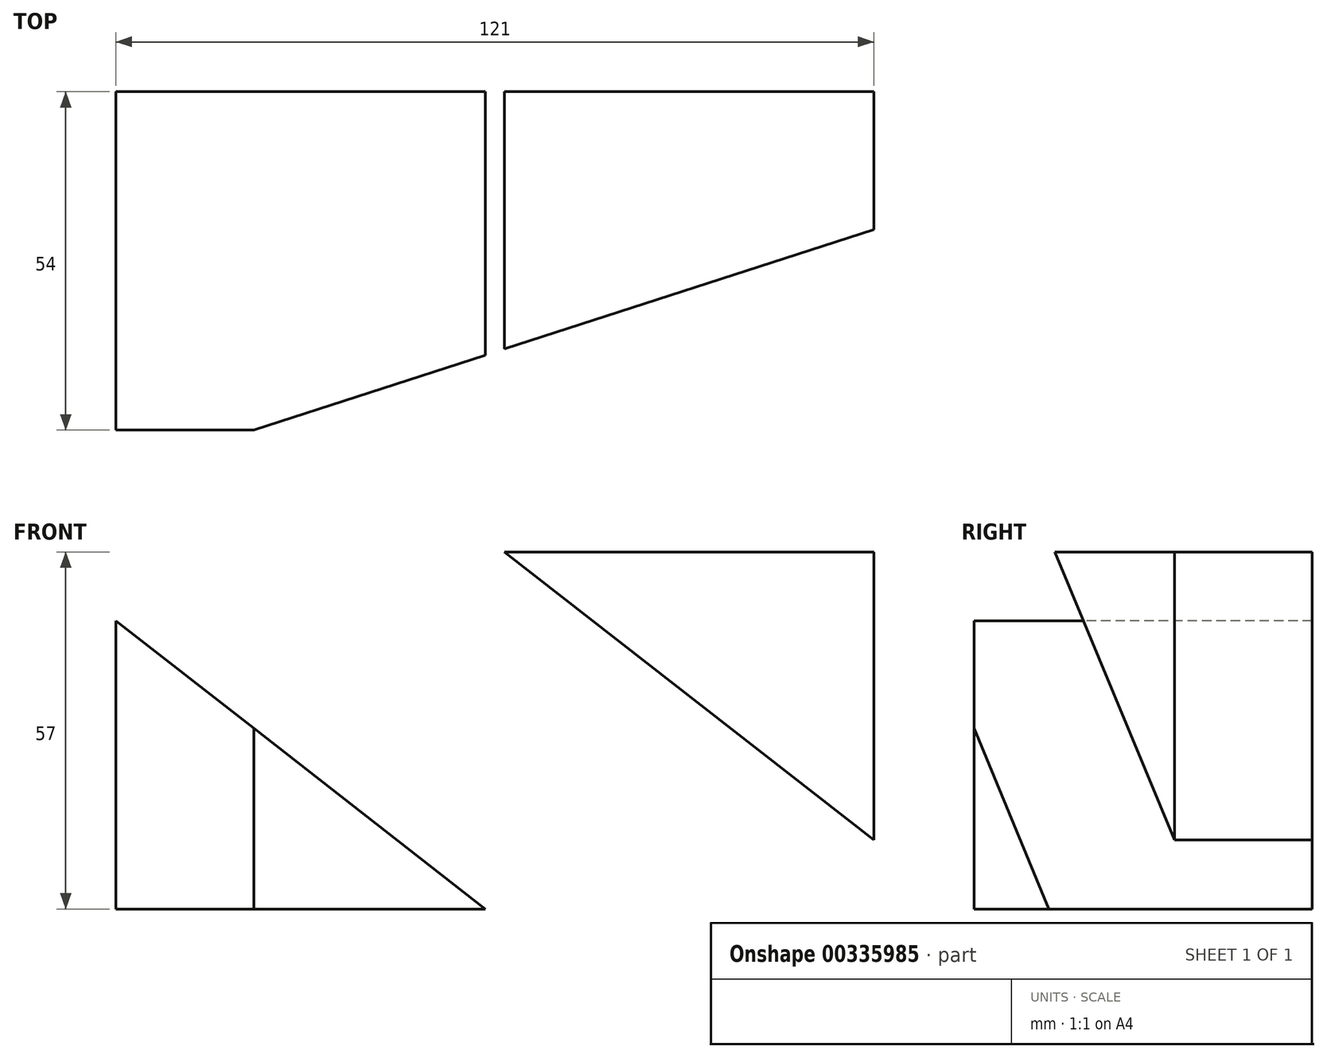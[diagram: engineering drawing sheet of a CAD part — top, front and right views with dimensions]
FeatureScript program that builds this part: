
annotation { "Feature Type Name" : "Feature", "Feature Type Description" : "" }
export const myFeature = defineFeature(function(context is Context, id is Id, definition is map)
    precondition{}
    {
        {
            var Q0;
            Q0=qCreatedBy(makeId("Front.planeOp"),FACE);
            var sketch = newSketch(context, id + "F0", { "sketchPlane" : qUnion([Q0])});
            skLineSegment(sketch, "E0", {"start": v(0, 0) * mm, "end": v(0, 57) * mm});
            skLineSegment(sketch, "E1", {"start": v(0, 0) * mm, "end": v(22, 0) * mm});
            skLineSegment(sketch, "E2", {"start": v(0, 57) * mm, "end": v(62, 57) * mm});
            skLineSegment(sketch, "E3", {"start": v(62, 57) * mm, "end": v(121, 57) * mm});
            skLineSegment(sketch, "E4", {"start": v(121, 57) * mm, "end": v(121, 11) * mm});
            skLineSegment(sketch, "E5", {"start": v(0, 0) * mm, "end": v(0, 46) * mm});
            skLineSegment(sketch, "E6", {"start": v(0, 46) * mm, "end": v(59, 0) * mm});
            skLineSegment(sketch, "E7", {"start": v(22, 0) * mm, "end": v(59, 0) * mm});
            skLineSegment(sketch, "E8", {"start": v(121, 11) * mm, "end": v(121, 0) * mm});
            skLineSegment(sketch, "E9", {"start": v(121, 0) * mm, "end": v(59, 0) * mm});
            skLineSegment(sketch, "E10", {"start": v(62, 57) * mm, "end": v(121, 11) * mm});
            skLineSegment(sketch, "E11", {"start": v(22, 0) * mm, "end": v(22, 28.85) * mm});
            skSolve(sketch);
        }
        {
            var Q0;
            Q0=makeQuery(id+"F0.imprint","IMPRINT",FACE,{"disambiguationData":[TD([[makeQuery(id+"F0.imprint","IMPRINT",EDGE,{"derivedFrom":sQuery(id+"F0.wireOp",EDGE,"E1")}),1.0]])]});
            var Q1;
            {var subQ0=sQuery(id+"F0.wireOp",EDGE,"E7");Q1=makeQuery(id+"F0.imprint","IMPRINT",FACE,{"disambiguationData":[TD([[makeQuery(id+"F0.imprint","IMPRINT",EDGE,{"derivedFrom":subQ0}),1.0]])]});}
            var Q2;
            {var subQ1=sQuery(id+"F0.wireOp",EDGE,"E0");Q2=makeQuery(id+"F0.imprint","IMPRINT",FACE,{"disambiguationData":[TD([[makeQuery(id+"F0.imprint","IMPRINT",EDGE,{"derivedFrom":subQ1}),-1.0]])]});}
            var Q3;
            Q3=makeQuery(id+"F0.imprint","IMPRINT",FACE,{"disambiguationData":[TD([[makeQuery(id+"F0.imprint","IMPRINT",EDGE,{"derivedFrom":sQuery(id+"F0.wireOp",EDGE,"E3")}),-1.0]])]});
            extrude(context, id + "F1", {"entities" : qUnion([Q0, Q1, Q2, Q3]), "oppositeDirection" : true, "depth" : 16 * mm});
        }
        {
            var Q0;
            Q0=makeQuery(id+"F0.imprint","IMPRINT",FACE,{"disambiguationData":[TD([[makeQuery(id+"F0.imprint","IMPRINT",EDGE,{"derivedFrom":sQuery(id+"F0.wireOp",EDGE,"E3")}),-1.0]])]});
            var Q1;
            {var subQ0=sQuery(id+"F0.wireOp",EDGE,"E7");Q1=makeQuery(id+"F0.imprint","IMPRINT",FACE,{"disambiguationData":[TD([[makeQuery(id+"F0.imprint","IMPRINT",EDGE,{"derivedFrom":subQ0}),1.0]])]});}
            var Q2;
            Q2=makeQuery(id+"F0.imprint","IMPRINT",FACE,{"disambiguationData":[TD([[makeQuery(id+"F0.imprint","IMPRINT",EDGE,{"derivedFrom":sQuery(id+"F0.wireOp",EDGE,"E1")}),1.0]])]});
            extrude(context, id + "F2", {"entities" : qUnion([Q0, Q1, Q2]), "operationType" : NewBodyOperationType.ADD, "depth" : 38 * mm});
        }
        {
            var Q0;
            {var subQ1=sQuery(id+"F0.wireOp",EDGE,"E0");Q0=makeQuery(id+"F0.imprint","IMPRINT",FACE,{"disambiguationData":[TD([[makeQuery(id+"F0.imprint","IMPRINT",EDGE,{"derivedFrom":subQ1}),-1.0]])]});}
            var sketch = newSketch(context, id + "F3", { "sketchPlane" : qUnion([Q0])});
            skLineSegment(sketch, "E12", {"start": v(0, 0) * mm, "end": v(44, 0) * mm, "construction": true});
            skLineSegment(sketch, "E13", {"start": v(44, 0) * mm, "end": v(44, 41) * mm, "construction": true});
            skLineSegment(sketch, "E14", {"start": v(44, 0) * mm, "end": v(77, 0) * mm, "construction": true});
            skLineSegment(sketch, "E15", {"start": v(77, 0) * mm, "end": v(77, 16) * mm, "construction": true});
            skCircle(sketch, "E16", {"center": v(44, 41) * mm, "radius": 7 * mm});
            skCircle(sketch, "E17", {"center": v(77, 16) * mm, "radius": 7 * mm});
            skSolve(sketch);
        }
        {
            var Q0;
            Q0=makeQuery(id+"F3.imprint","IMPRINT",FACE,{"disambiguationData":[TD([[makeQuery(id+"F3.imprint","IMPRINT",EDGE,{"derivedFrom":sQuery(id+"F3.wireOp",EDGE,"E17")}),1.0]])]});
            var Q1;
            Q1=makeQuery(id+"F3.imprint","IMPRINT",FACE,{"disambiguationData":[TD([[makeQuery(id+"F3.imprint","IMPRINT",EDGE,{"derivedFrom":sQuery(id+"F3.wireOp",EDGE,"E16")}),1.0]])]});
            var Q2;
            Q2=sQuery(id+"F3.wireOp",EDGE,"E16");
            var Q3;
            Q3=sQuery(id+"F3.wireOp",EDGE,"E17");
            extrude(context, id + "F4", {"entities" : qUnion([Q0, Q1]), "operationType" : NewBodyOperationType.REMOVE, "surfaceEntities" : qUnion([Q2, Q3]), "oppositeDirection" : true, "depth" : 25 * mm});
        }
        {
            var Q0;
            {var subQ0=sQuery(id+"F0.wireOp",EDGE,"E3");Q0=makeQuery(id+"F2.boolean.opBoolean","MERGE",FACE,{"derivedFrom":[makeQuery(id+"F1.opExtrude","SWEPT_FACE",FACE,{"disambiguationData":[OSD([sQuery(id+"F0.wireOp",EDGE,"E2"),subQ0])]}),makeQuery(id+"F2.opExtrude","SWEPT_FACE",FACE,{"disambiguationData":[OSD([subQ0])]})]});}
            var sketch = newSketch(context, id + "F5", { "sketchPlane" : qUnion([Q0])});
            skLineSegment(sketch, "E18", {"start": v(121, 16) * mm, "end": v(0, 16) * mm});
            skLineSegment(sketch, "E19", {"start": v(0, 16) * mm, "end": v(0, -38) * mm});
            skLineSegment(sketch, "E20", {"start": v(0, -38) * mm, "end": v(22, -38) * mm});
            skLineSegment(sketch, "E21", {"start": v(22, -38) * mm, "end": v(121, -6) * mm});
            skLineSegment(sketch, "E22", {"start": v(121, -6) * mm, "end": v(121, 16) * mm});
            skLineSegment(sketch, "E23", {"start": v(22, -38) * mm, "end": v(121, -38) * mm});
            skLineSegment(sketch, "E24", {"start": v(121, -38) * mm, "end": v(121, -6) * mm});
            skSolve(sketch);
        }
        {
            var Q0;
            {var subQ0=sQuery(id+"F5.wireOp",EDGE,"E24");Q0=makeQuery(id+"F5.imprint","IMPRINT",FACE,{"disambiguationData":[TD([[makeQuery(id+"F5.imprint","IMPRINT",EDGE,{"derivedFrom":subQ0}),-1.0]])]});}
            var Q1;
            {var subQ0=sQuery(id+"F5.wireOp",EDGE,"E23");var subQ1=sQuery(id+"F5.wireOp",EDGE,"E21");var subQ2=makeQuery(id+"F5.imprint","INTERSECT",VERTEX,{"derivedFrom":[sQuery(id+"F5.wireOp",EDGE,"E20"),subQ1,subQ0]});Q1=makeQuery(id+"F5.imprint","IMPRINT",FACE,{"disambiguationData":[TD([[makeQuery(id+"F5.imprint","IMPRINT",EDGE,{"disambiguationData":[TD([[subQ2,-1.0]])],"derivedFrom":subQ1}),-1.0]])]});}
            extrude(context, id + "F6", {"entities" : qUnion([Q0, Q1]), "operationType" : NewBodyOperationType.REMOVE, "oppositeDirection" : true, "depth" : 57 * mm});
        }
    });
